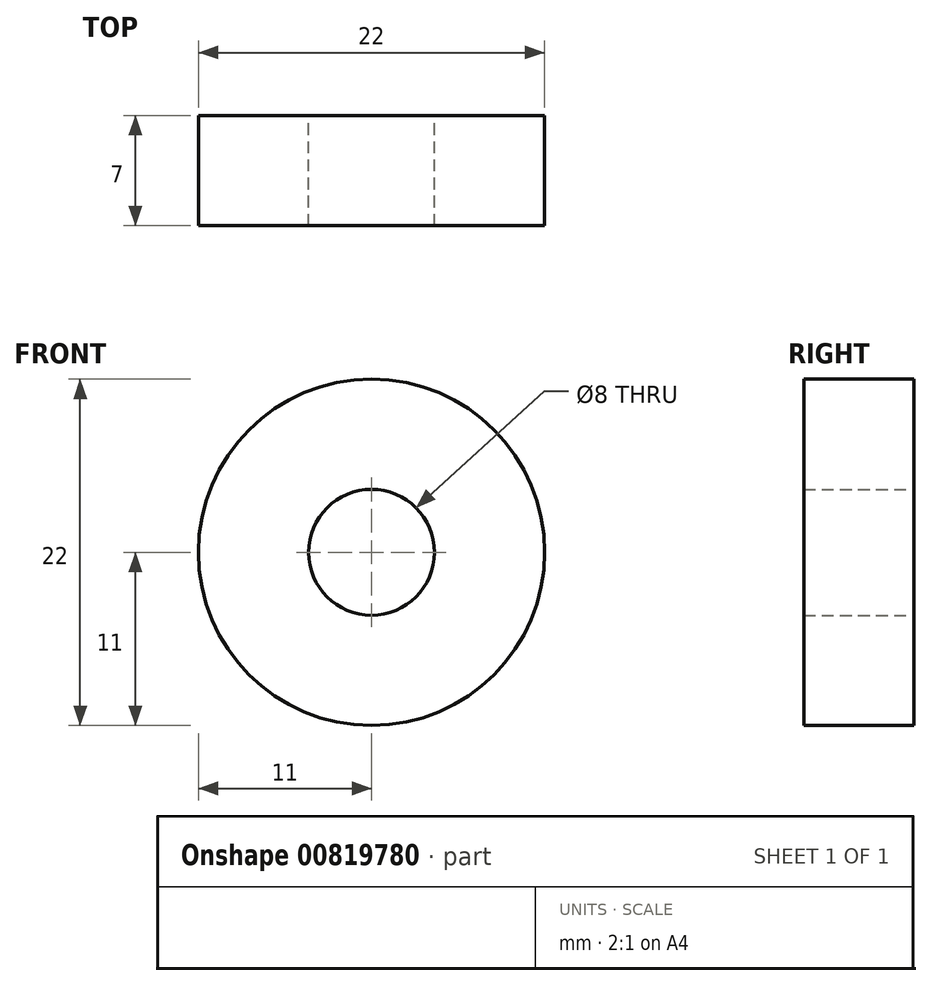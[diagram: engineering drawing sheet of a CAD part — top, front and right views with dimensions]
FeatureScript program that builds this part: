
annotation { "Feature Type Name" : "Feature", "Feature Type Description" : "" }
export const myFeature = defineFeature(function(context is Context, id is Id, definition is map)
    precondition{}
    {
        {
            var Q0;
            Q0=qCreatedBy(makeId("Front.planeOp"),FACE);
            var sketch = newSketch(context, id + "F0", { "sketchPlane" : qUnion([Q0])});
            skCircle(sketch, "E0", {"center": v(0, 0) * mm, "radius": 11 * mm});
            skCircle(sketch, "E1", {"center": v(0, 0) * mm, "radius": 4 * mm});
            skSolve(sketch);
        }
        {
            var Q0;
            Q0=makeQuery(id+"F0.imprint","IMPRINT",FACE,{"disambiguationData":[TD([[makeQuery(id+"F0.imprint","IMPRINT",EDGE,{"derivedFrom":sQuery(id+"F0.wireOp",EDGE,"E0")}),1.0]])]});
            extrude(context, id + "F1", {"entities" : qUnion([Q0]), "depth" : 7 * mm, "offsetDistance" : 25 * mm});
        }
    });
